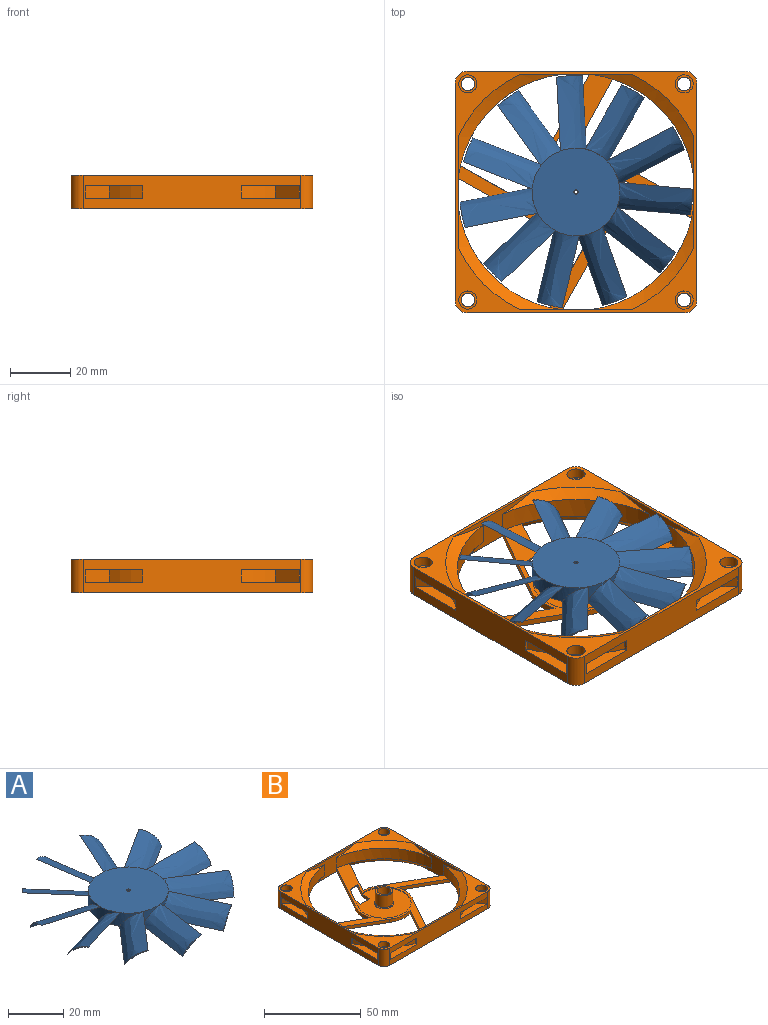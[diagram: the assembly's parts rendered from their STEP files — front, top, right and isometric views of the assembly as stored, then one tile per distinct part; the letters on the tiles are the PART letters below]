
ASSEMBLY  parts=2 mates=1
PART A: 55 faces, bbox 76.7x77.4x9.3 mm
  f0: cylinder r=1mm len=7.2mm, axis (0,0,1), area 45.2mm2, adj f1,f49
  f1: plane 23x23mm, normal (0,0,-1), area 412.3mm2, adj f0,f24
  f2: extruded ~24.7x8.56mm, area 264.1mm2, adj f3,f35,f48
  f3: extruded ~24.7x8.56mm, area 257.7mm2, adj f2,f25,f48
  f4: extruded ~25.4x20.55mm, area 264.1mm2, adj f5,f34,f47
  f5: extruded ~25.4x20.55mm, area 257.7mm2, adj f4,f35,f47
  f6: extruded ~26.02x18.04mm, area 257.7mm2, adj f7,f34,f46
  f7: extruded ~26.02x18.04mm, area 264.1mm2, adj f6,f33,f46
  f8: extruded ~25.66x11.98mm, area 257.7mm2, adj f9,f33,f45
  f9: extruded ~25.66x11.98mm, area 264.1mm2, adj f8,f32,f45
  f10: extruded ~24.27x22.64mm, area 257.7mm2, adj f11,f32,f44
  f11: extruded ~24.27x22.64mm, area 264.1mm2, adj f10,f31,f44
  f12: extruded ~26.11x15.17mm, area 257.7mm2, adj f13,f31,f43
  f13: extruded ~26.11x15.17mm, area 264.1mm2, adj f12,f30,f43
  f14: extruded ~26.11x15.17mm, area 257.7mm2, adj f15,f30,f42
  f15: extruded ~26.11x15.17mm, area 264.1mm2, adj f14,f29,f42
  f16: extruded ~24.27x22.64mm, area 257.7mm2, adj f17,f29,f41
  f17: extruded ~24.27x22.64mm, area 264.1mm2, adj f16,f28,f41
  f18: extruded ~25.66x11.98mm, area 257.7mm2, adj f19,f28,f40
  f19: extruded ~25.66x11.98mm, area 264.1mm2, adj f18,f27,f40
  f20: extruded ~26.02x18.04mm, area 257.7mm2, adj f21,f27,f39
  f21: extruded ~26.02x18.04mm, area 264.1mm2, adj f20,f26,f39
  f22: extruded ~25.4x20.55mm, area 257.7mm2, adj f23,f26,f38
  f23: extruded ~25.4x20.55mm, area 264.1mm2, adj f22,f25,f38
  f24: cylinder r=11.5mm len=23mm, axis (0,0,-1), area 361.3mm2, adj f1,f37
  f25: cylinder r=14.5mm len=15.31mm, axis (0,0,-1), area 46.5mm2, adj f3,f23,f36,f37
  f26: cylinder r=14.5mm len=12.23mm, axis (0,0,-1), area 46.5mm2, adj f21,f22,f36,f37
  f27: cylinder r=14.5mm len=15.88mm, axis (0,0,-1), area 46.5mm2, adj f19,f20,f36,f37
  f28: cylinder r=14.5mm len=14.49mm, axis (0,0,-1), area 46.5mm2, adj f17,f18,f36,f37
  f29: cylinder r=14.5mm len=13.57mm, axis (0,0,-1), area 46.5mm2, adj f15,f16,f36,f37
  f30: cylinder r=14.5mm len=16.01mm, axis (0,0,-1), area 46.5mm2, adj f13,f14,f36,f37
  f31: cylinder r=14.5mm len=13.37mm, axis (0,0,-1), area 46.5mm2, adj f11,f12,f36,f37
  f32: cylinder r=14.5mm len=14.65mm, axis (0,0,-1), area 46.5mm2, adj f9,f10,f36,f37
  f33: cylinder r=14.5mm len=15.83mm, axis (0,0,-1), area 46.5mm2, adj f7,f8,f36,f37
  f34: cylinder r=14.5mm len=11.98mm, axis (0,0,-1), area 46.5mm2, adj f4,f6,f36,f37
  f35: cylinder r=14.5mm len=15.42mm, axis (0,0,-1), area 46.5mm2, adj f2,f5,f36,f37
  f36: plane 29x29mm, normal (0,0,1), area 659mm2, adj f25,f26,f27,f28,f29,f30,f31,f32
  f37: plane 29x29mm, normal (0,0,-1), area 245mm2, adj f24,f25,f26,f27,f28,f29,f30,f31
  f38: cylinder r=38.5mm len=7.18mm, axis (0,0,1), area 3.2mm2, adj f22,f23
  f39: cylinder r=38.5mm len=7.8mm, axis (0,0,1), area 3.2mm2, adj f20,f21
  f40: cylinder r=38.5mm len=8.46mm, axis (0,0,1), area 3.2mm2, adj f18,f19
  f41: cylinder r=38.5mm len=6.44mm, axis (0,0,1), area 3.2mm2, adj f16,f17
  f42: cylinder r=38.5mm len=8.22mm, axis (0,0,1), area 3.2mm2, adj f14,f15
  f43: cylinder r=38.5mm len=8.2mm, axis (0,0,1), area 3.2mm2, adj f12,f13
  f44: cylinder r=38.5mm len=6.49mm, axis (0,0,1), area 3.2mm2, adj f10,f11
  f45: cylinder r=38.5mm len=8.47mm, axis (0,0,1), area 3.2mm2, adj f8,f9
  f46: cylinder r=38.5mm len=7.77mm, axis (0,0,1), area 3.2mm2, adj f6,f7
  f47: cylinder r=38.5mm len=7.22mm, axis (0,0,1), area 3.2mm2, adj f4,f5
  f48: cylinder r=38.5mm len=8.56mm, axis (0,0,1), area 3.2mm2, adj f2,f3
  f49: plane 2x2mm, normal (0,0,-1), area 1.4mm2, adj f0,f50
  f50: cylinder r=0.75mm len=1.5mm, axis (0,0,-1), area 1.4mm2, adj f49,f51
  f51: plane 2x2mm, normal (0,0,1), area 1.4mm2, adj f50,f52
  f52: cylinder r=1mm len=2mm, axis (0,0,1), area 3.1mm2, adj f51,f53
  f53: cone r=0.5mm half-angle=45deg, axis (0,0,1), area 2.3mm2, adj f52,f54
  f54: cylinder r=0.7mm len=9.3mm, axis (0,0,1), area 40.9mm2, adj f36,f53
PART B: 114 faces, bbox 85.7x85.7x11 mm
  f0: cylinder r=3mm len=6mm, axis (0,0,1), area 66mm2, adj f1,f21
  f1: plane 6x6mm, normal (0,0,1), area 12.4mm2, adj f0,f20
  f2: cylinder r=3mm len=6mm, axis (0,0,1), area 66mm2, adj f3,f21
  f3: plane 6x6mm, normal (0,0,1), area 12.4mm2, adj f2,f18
  f4: cylinder r=3mm len=6mm, axis (0,0,1), area 66mm2, adj f5,f21
  f5: plane 6x6mm, normal (0,0,1), area 12.4mm2, adj f4,f19
  f6: plane 6x6mm, normal (0,0,1), area 12.4mm2, adj f7,f17
  f7: cylinder r=3mm len=6mm, axis (0,0,1), area 66mm2, adj f6,f21
  f8: plane 5.63x1.5mm, normal (-1,0,0), area 8.4mm2, adj f9,f22,f61,f108
  f9: plane 6.65x1.5mm, normal (0,1,0), area 10mm2, adj f8,f22,f62,f108
  f10: plane 77.99x77.99mm, normal (0,0,1), area 636.1mm2, adj f11,f13,f15,f31,f45,f46,f47,f48
  f11: cylinder r=39.25mm len=34.58mm, axis (0,0,-1), area 357.4mm2, adj f10,f12,f22,f43,f44,f50,f113
  f12: cone r=39.25mm half-angle=60deg, axis (0,0,1), area 172.8mm2, adj f11,f21,f43,f44
  f13: cylinder r=39.25mm len=34.58mm, axis (0,0,-1), area 357.4mm2, adj f10,f14,f22,f42,f43,f53,f110
  f14: cone r=39.25mm half-angle=60deg, axis (0,0,1), area 172.8mm2, adj f13,f21,f42,f43
  f15: cylinder r=39.25mm len=34.58mm, axis (0,0,-1), area 357.4mm2, adj f10,f16,f22,f41,f42,f56,f111
  f16: cone r=39.25mm half-angle=60deg, axis (0,0,1), area 172.8mm2, adj f15,f21,f41,f42
  f17: cylinder r=2.25mm len=4.5mm, axis (0,0,1), area 56.5mm2, adj f6,f38
  f18: cylinder r=2.25mm len=4.5mm, axis (0,0,-1), area 56.5mm2, adj f3,f37
  f19: cylinder r=2.25mm len=4.5mm, axis (0,0,-1), area 56.5mm2, adj f5,f35
  f20: cylinder r=2.25mm len=4.5mm, axis (0,0,1), area 56.5mm2, adj f1,f32
  f21: plane 80x80mm, normal (0,0,1), area 840.6mm2, adj f0,f2,f4,f7,f12,f14,f16,f23
  f22: plane 80x80mm, normal (0,0,-1), area 2305.9mm2, adj f8,f9,f11,f13,f15,f23,f24,f25
  f23: cylinder r=4mm len=11mm, axis (0,0,-1), area 69.1mm2, adj f21,f22,f24,f30
  f24: plane 72x11mm, normal (-1,0,0), area 639.3mm2, adj f21,f22,f23,f25,f72,f74,f75,f76
  f25: cylinder r=4mm len=11mm, axis (0,0,-1), area 69.1mm2, adj f21,f22,f24,f26
  f26: plane 72x11mm, normal (0,-1,0), area 639.3mm2, adj f21,f22,f25,f27,f88,f89,f90,f91
  f27: cylinder r=4mm len=11mm, axis (0,0,-1), area 69.1mm2, adj f21,f22,f26,f28
  f28: plane 72x11mm, normal (1,0,0), area 639.3mm2, adj f21,f22,f27,f29,f78,f79,f80,f81
  f29: cylinder r=4mm len=11mm, axis (0,0,-1), area 69.1mm2, adj f21,f22,f28,f30
  f30: plane 72x11mm, normal (0,1,0), area 630.7mm2, adj f21,f22,f23,f29,f64,f65,f66,f68
  f31: cylinder r=39.25mm len=34.58mm, axis (0,0,-1), area 357.4mm2, adj f10,f22,f40,f41,f44,f47,f112
  f32: plane 6x6mm, normal (0,0,-1), area 12.4mm2, adj f20,f33
  f33: cylinder r=3mm len=6mm, axis (0,0,-1), area 66mm2, adj f22,f32
  f34: cylinder r=3mm len=6mm, axis (0,0,-1), area 66mm2, adj f22,f35
  f35: plane 6x6mm, normal (0,0,-1), area 12.4mm2, adj f19,f34
  f36: cylinder r=3mm len=6mm, axis (0,0,-1), area 66mm2, adj f22,f37
  f37: plane 6x6mm, normal (0,0,-1), area 12.4mm2, adj f18,f36
  f38: plane 6x6mm, normal (0,0,-1), area 12.4mm2, adj f17,f39
  f39: cylinder r=3mm len=6mm, axis (0,0,-1), area 66mm2, adj f22,f38
  f40: cone r=39.25mm half-angle=60deg, axis (0,0,1), area 172.8mm2, adj f21,f31,f41,f44
  f41: plane 36.78x11.01mm, normal (1,0,0), area 141.3mm2, adj f15,f16,f21,f22,f31,f40,f112
  f42: plane 36.78x11.01mm, normal (0,-1,0), area 141.3mm2, adj f13,f14,f15,f16,f21,f22,f111
  f43: plane 36.78x11.01mm, normal (-1,0,0), area 141.3mm2, adj f11,f12,f13,f14,f21,f22,f110
  f44: plane 36.78x11.01mm, normal (0,1,0), area 141.3mm2, adj f11,f12,f21,f22,f31,f40,f113
  f45: cylinder r=15.25mm len=13.27mm, axis (0,0,-1), area 27.8mm2, adj f10,f22,f46,f56
  f46: plane 24.83x13.94mm, normal (-0.87,0.49,0), area 55.7mm2, adj f10,f22,f45,f112
  f47: plane 30.41x17.07mm, normal (0.87,-0.49,0), area 69.7mm2, adj f10,f22,f31,f48
  f48: cylinder r=15.25mm len=13.27mm, axis (0,0,-1), area 27.8mm2, adj f10,f22,f47,f49
  f49: plane 24.83x13.94mm, normal (-0.49,-0.87,0), area 55.7mm2, adj f10,f22,f48,f113
  f50: plane 30.41x17.07mm, normal (0.49,0.87,0), area 69.7mm2, adj f10,f11,f22,f51
  f51: cylinder r=15.25mm len=8.56mm, axis (0,0,-1), area 18.2mm2, adj f10,f22,f50,f52
  f52: plane 23.14x12.59mm, normal (0.88,-0.48,0), area 51.5mm2, adj f10,f22,f51,f110
  f53: plane 30.41x17.07mm, normal (-0.87,0.49,0), area 69.7mm2, adj f10,f13,f22,f54
  f54: cylinder r=15.25mm len=13.27mm, axis (0,0,-1), area 27.8mm2, adj f10,f22,f53,f55
  f55: plane 24.83x13.94mm, normal (0.49,0.87,0), area 55.7mm2, adj f10,f22,f54,f111
  f56: plane 30.41x17.07mm, normal (-0.49,-0.87,0), area 69.7mm2, adj f10,f15,f22,f45
  f57: cylinder r=4.5mm len=9mm, axis (0,0,-1), area 212.1mm2, adj f58,f109
  f58: plane 9x9mm, normal (0,0,1), area 25.1mm2, adj f57,f59
  f59: cylinder r=3.5mm len=9.5mm, axis (0,0,1), area 208.9mm2, adj f22,f58
  f60: plane 5.73x0.5mm, normal (0,-1,0), area 2.9mm2, adj f10,f61,f63,f66
  f61: plane 7.37x4.14mm, normal (-0.87,0.49,0), area 16.8mm2, adj f8,f10,f22,f60,f64,f107,f108
  f62: plane 4x2mm, normal (1,0,0), area 6.6mm2, adj f9,f10,f22,f63,f107,f108
  f63: plane 9x5.05mm, normal (0.87,-0.49,0), area 20.6mm2, adj f10,f22,f60,f62,f65
  f64: plane 19.05x10.47mm, normal (-0.88,0.48,0), area 32.6mm2, adj f22,f30,f61,f66
  f65: plane 19.05x10.47mm, normal (0.88,-0.48,0), area 32.6mm2, adj f22,f30,f63,f66
  f66: plane 19.05x16.2mm, normal (0,0,-1), area 109.2mm2, adj f30,f60,f64,f65
  f67: cylinder r=42.25mm len=11.28mm, axis (0,0,-1), area 53.2mm2, adj f68,f69,f70,f71
  f68: plane 4x1mm, normal (-1,0,0), area 4mm2, adj f30,f67,f70,f71
  f69: plane 7.95x7.95mm, normal (0.71,0.71,0), area 45mm2, adj f30,f67,f70,f71
  f70: plane 19.22x7.95mm, normal (0,0,-1), area 77.4mm2, adj f30,f67,f68,f69
  f71: plane 19.22x7.95mm, normal (0,0,1), area 77.4mm2, adj f30,f67,f68,f69
  f72: plane 4x1mm, normal (0,1,0), area 4mm2, adj f24,f73,f75,f76
  f73: cylinder r=42.25mm len=11.12mm, axis (0,0,-1), area 52.4mm2, adj f72,f74,f75,f76
  f74: plane 7.82x7.82mm, normal (-0.71,-0.71,0), area 44.2mm2, adj f24,f73,f75,f76
  f75: plane 18.94x7.82mm, normal (0,0,-1), area 75.2mm2, adj f24,f72,f73,f74
  f76: plane 18.94x7.82mm, normal (0,0,1), area 75.2mm2, adj f24,f72,f73,f74
  f77: cylinder r=42.25mm len=11.28mm, axis (0,0,-1), area 53.2mm2, adj f78,f79,f80,f81
  f78: plane 4x1mm, normal (0,1,0), area 4mm2, adj f28,f77,f80,f81
  f79: plane 7.95x7.95mm, normal (0.71,-0.71,0), area 45mm2, adj f28,f77,f80,f81
  f80: plane 19.22x7.95mm, normal (0,0,-1), area 77.4mm2, adj f28,f77,f78,f79
  f81: plane 19.22x7.95mm, normal (0,0,1), area 77.4mm2, adj f28,f77,f78,f79
  f82: plane 4x1mm, normal (1,0,0), area 4mm2, adj f30,f83,f85,f86
  f83: cylinder r=42.25mm len=11.12mm, axis (0,0,-1), area 52.4mm2, adj f82,f84,f85,f86
  f84: plane 7.82x7.82mm, normal (-0.71,0.71,0), area 44.2mm2, adj f30,f83,f85,f86
  f85: plane 18.94x7.82mm, normal (0,0,-1), area 75.2mm2, adj f30,f82,f83,f84
  f86: plane 18.94x7.82mm, normal (0,0,1), area 75.2mm2, adj f30,f82,f83,f84
  f87: cylinder r=42.25mm len=11.28mm, axis (0,0,-1), area 53.2mm2, adj f88,f89,f90,f91
  f88: plane 4x1mm, normal (1,0,0), area 4mm2, adj f26,f87,f90,f91
  f89: plane 7.95x7.95mm, normal (-0.71,-0.71,0), area 45mm2, adj f26,f87,f90,f91
  f90: plane 19.22x7.95mm, normal (0,0,-1), area 77.4mm2, adj f26,f87,f88,f89
  f91: plane 19.22x7.95mm, normal (0,0,1), area 77.4mm2, adj f26,f87,f88,f89
  f92: plane 4x1mm, normal (0,-1,0), area 4mm2, adj f28,f93,f95,f96
  f93: cylinder r=42.25mm len=11.12mm, axis (0,0,-1), area 52.4mm2, adj f92,f94,f95,f96
  f94: plane 7.82x7.82mm, normal (0.71,0.71,0), area 44.2mm2, adj f28,f93,f95,f96
  f95: plane 18.94x7.82mm, normal (0,0,-1), area 75.2mm2, adj f28,f92,f93,f94
  f96: plane 18.94x7.82mm, normal (0,0,1), area 75.2mm2, adj f28,f92,f93,f94
  f97: cylinder r=42.25mm len=11.28mm, axis (0,0,-1), area 53.2mm2, adj f98,f99,f100,f101
  f98: plane 4x1mm, normal (0,-1,0), area 4mm2, adj f24,f97,f100,f101
  f99: plane 7.95x7.95mm, normal (-0.71,0.71,0), area 45mm2, adj f24,f97,f100,f101
  f100: plane 19.22x7.95mm, normal (0,0,-1), area 77.4mm2, adj f24,f97,f98,f99
  f101: plane 19.22x7.95mm, normal (0,0,1), area 77.4mm2, adj f24,f97,f98,f99
  f102: plane 4x1mm, normal (-1,0,0), area 4mm2, adj f26,f103,f105,f106
  f103: cylinder r=42.25mm len=11.12mm, axis (0,0,-1), area 52.4mm2, adj f102,f104,f105,f106
  f104: plane 7.82x7.82mm, normal (0.71,-0.71,0), area 44.2mm2, adj f26,f103,f105,f106
  f105: plane 18.94x7.82mm, normal (0,0,-1), area 75.2mm2, adj f26,f102,f103,f104
  f106: plane 18.94x7.82mm, normal (0,0,1), area 75.2mm2, adj f26,f102,f103,f104
  f107: cylinder r=14mm len=28mm, axis (0,0,1), area 40.2mm2, adj f10,f61,f62,f108
  f108: plane 28x28mm, normal (0,0,1), area 506.1mm2, adj f8,f9,f61,f62,f107,f109
  f109: cone r=4.5mm half-angle=45deg, axis (0,0,-1), area 21.1mm2, adj f57,f108
  f110: cone r=40.12mm half-angle=30deg, axis (0,0,-1), area 97.2mm2, adj f13,f22,f43,f52
  f111: cone r=40.12mm half-angle=30deg, axis (0,0,-1), area 105.2mm2, adj f15,f22,f42,f55
  f112: cone r=40.12mm half-angle=30deg, axis (0,0,-1), area 105.2mm2, adj f22,f31,f41,f46
  f113: cone r=40.12mm half-angle=30deg, axis (0,0,-1), area 105.2mm2, adj f11,f22,f44,f49
PLACE A rot(axis=(0,0,1),60.2deg) t=(0,0,5)mm
PLACE B at identity fixed
MATE revolute B.f11 <-> A.f0  axis (0,0,1) through (0,0,2)mm
